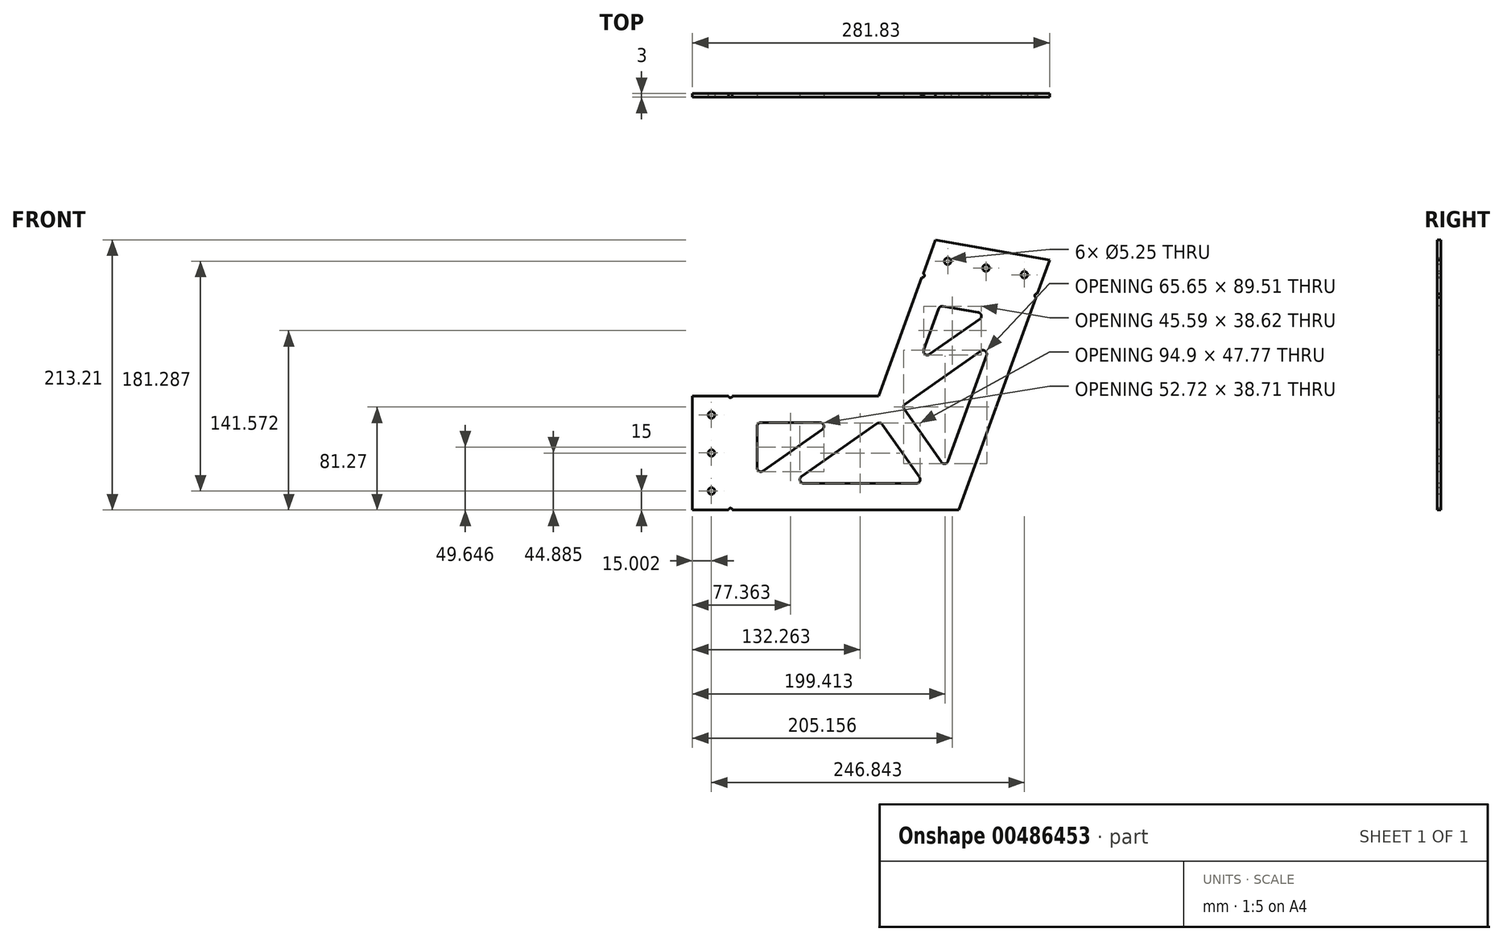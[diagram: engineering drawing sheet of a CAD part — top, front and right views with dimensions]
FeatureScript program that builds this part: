
annotation { "Feature Type Name" : "Feature", "Feature Type Description" : "" }
export const myFeature = defineFeature(function(context is Context, id is Id, definition is map)
    precondition{}
    {
        {
            var Q0;
            Q0=qCreatedBy(makeId("Front.planeOp"),FACE);
            var sketch = newSketch(context, id + "F0", { "sketchPlane" : qUnion([Q0])});
            skLineSegment(sketch, "E0", {"start": v(0, 0) * mm, "end": v(0, 0) * mm});
            skLineSegment(sketch, "E1", {"start": v(50, -65) * mm, "end": v(70.35, -9.1) * mm});
            skLineSegment(sketch, "E2", {"start": v(50, -65) * mm, "end": v(-9.5, -65) * mm});
            skLineSegment(sketch, "E3.0", {"start": v(29, -35) * mm, "end": v(40.35, -3.8) * mm});
            skLineSegment(sketch, "E4", {"start": v(-9.5, -35) * mm, "end": v(29, -35) * mm});
            skLineSegment(sketch, "E5.0", {"start": v(40.85, -22.91) * mm, "end": v(44.8, -12.04) * mm});
            skLineSegment(sketch, "E5.1", {"start": v(47.22, -52.19) * mm, "end": v(57.35, -24.34) * mm});
            skLineSegment(sketch, "E5.2", {"start": v(38.9, -58) * mm, "end": v(9.27, -58) * mm});
            skLineSegment(sketch, "E5.3", {"start": v(45.92, -11.4) * mm, "end": v(55.16, -13.03) * mm});
            skLineSegment(sketch, "E5.4", {"start": v(-3, -53.91) * mm, "end": v(-3, -43) * mm});
            skLineSegment(sketch, "E5.5", {"start": v(-2, -42) * mm, "end": v(13.57, -42) * mm});
            skLineSegment(sketch, "E6.0.left", {"start": v(-1.43, -54.73) * mm, "end": v(14.15, -43.83) * mm});
            skLineSegment(sketch, "E6.0.right", {"start": v(8.7, -56.2) * mm, "end": v(28.58, -42.27) * mm});
            skLineSegment(sketch, "E7.trimOffspring", {"start": v(42.36, -24.07) * mm, "end": v(55.56, -14.83) * mm});
            skLineSegment(sketch, "E8.0.left", {"start": v(35.7, -38.5) * mm, "end": v(45.46, -52.42) * mm});
            skLineSegment(sketch, "E8.0.right", {"start": v(29.97, -42.51) * mm, "end": v(39.72, -56.44) * mm});
            skLineSegment(sketch, "E9.trimOffspring", {"start": v(35.95, -37.1) * mm, "end": v(55.84, -23.18) * mm});
            skPoint(sketch, "E10.visualSharp", {"position": v(-3, -55.84) * mm});
            skArc(sketch, "E10.filletArc", {"start": v(-3, -53.91) * mm, "mid": v(-2.46, -54.8) * mm, "end": v(-1.43, -54.73) * mm});
            skPoint(sketch, "E11.visualSharp", {"position": v(-3, -42) * mm});
            skArc(sketch, "E11.filletArc", {"start": v(-2, -42) * mm, "mid": v(-2.7, -42.3) * mm, "end": v(-3, -43) * mm});
            skPoint(sketch, "E12.visualSharp", {"position": v(16.75, -42) * mm});
            skArc(sketch, "E12.filletArc", {"start": v(14.15, -43.83) * mm, "mid": v(14.53, -42.7) * mm, "end": v(13.57, -42) * mm});
            skPoint(sketch, "E13.visualSharp", {"position": v(29.4, -41.7) * mm});
            skArc(sketch, "E13.filletArc", {"start": v(29.97, -42.51) * mm, "mid": v(29.33, -42.1) * mm, "end": v(28.58, -42.27) * mm});
            skPoint(sketch, "E14.visualSharp", {"position": v(6.1, -58) * mm});
            skArc(sketch, "E14.filletArc", {"start": v(8.7, -56.2) * mm, "mid": v(8.32, -57.31) * mm, "end": v(9.27, -58) * mm});
            skPoint(sketch, "E15.visualSharp", {"position": v(40.83, -58) * mm});
            skArc(sketch, "E15.filletArc", {"start": v(38.9, -58) * mm, "mid": v(39.8, -57.47) * mm, "end": v(39.72, -56.44) * mm});
            skPoint(sketch, "E16.visualSharp", {"position": v(46.56, -54) * mm});
            skArc(sketch, "E16.filletArc", {"start": v(45.46, -52.42) * mm, "mid": v(46.4, -52.84) * mm, "end": v(47.22, -52.19) * mm});
            skPoint(sketch, "E17.visualSharp", {"position": v(35.14, -37.68) * mm});
            skArc(sketch, "E17.filletArc", {"start": v(35.95, -37.1) * mm, "mid": v(35.54, -37.75) * mm, "end": v(35.7, -38.5) * mm});
            skPoint(sketch, "E18.visualSharp", {"position": v(58.44, -21.36) * mm});
            skArc(sketch, "E18.filletArc", {"start": v(57.35, -24.34) * mm, "mid": v(57.02, -23.2) * mm, "end": v(55.84, -23.18) * mm});
            skPoint(sketch, "E19.visualSharp", {"position": v(45.1, -11.25) * mm});
            skArc(sketch, "E19.filletArc", {"start": v(45.92, -11.4) * mm, "mid": v(45.24, -11.52) * mm, "end": v(44.8, -12.04) * mm});
            skPoint(sketch, "E20.visualSharp", {"position": v(39.76, -25.9) * mm});
            skArc(sketch, "E20.filletArc", {"start": v(40.85, -22.91) * mm, "mid": v(41.18, -24.05) * mm, "end": v(42.36, -24.07) * mm});
            skPoint(sketch, "E21.visualSharp", {"position": v(57.54, -13.45) * mm});
            skArc(sketch, "E21.filletArc", {"start": v(55.56, -14.83) * mm, "mid": v(55.96, -13.8) * mm, "end": v(55.16, -13.03) * mm});
            skLineSegment(sketch, "E22", {"start": v(-10.5, -35) * mm, "end": v(-20, -35) * mm});
            skLineSegment(sketch, "E23", {"start": v(-10.5, -65) * mm, "end": v(-20, -65) * mm});
            skLineSegment(sketch, "E24", {"start": v(-20, -65) * mm, "end": v(-20, -35) * mm});
            skLineSegment(sketch, "E25", {"start": v(40.7, -2.87) * mm, "end": v(43.94, 6.06) * mm});
            skLineSegment(sketch, "E26", {"start": v(70.7, -8.16) * mm, "end": v(73.94, 0.77) * mm});
            skLineSegment(sketch, "E27", {"start": v(43.94, 6.06) * mm, "end": v(73.94, 0.77) * mm});
            skArc(sketch, "E28", {"start": v(-10.5, -35) * mm, "mid": v(-10, -35.5) * mm, "end": v(-9.5, -35) * mm});
            skArc(sketch, "E29", {"start": v(-9.5, -65) * mm, "mid": v(-10, -64.5) * mm, "end": v(-10.5, -65) * mm});
            skArc(sketch, "E30", {"start": v(40.35, -3.8) * mm, "mid": v(41, -3.5) * mm, "end": v(40.7, -2.87) * mm});
            skArc(sketch, "E31", {"start": v(70.7, -8.16) * mm, "mid": v(70.05, -8.46) * mm, "end": v(70.35, -9.1) * mm});
            skCircle(sketch, "E32", {"center": v(-15, -40) * mm, "radius": 0.88 * mm});
            skPoint(sketch, "E32.centerSnap0", {"position": v(-15.25, -35) * mm});
            skCircle(sketch, "E33", {"center": v(-15, -60) * mm, "radius": 0.88 * mm});
            skCircle(sketch, "E34", {"center": v(-15, -50) * mm, "radius": 0.88 * mm});
            skCircle(sketch, "E35", {"center": v(57.2, -1.36) * mm, "radius": 0.88 * mm});
            skCircle(sketch, "E36", {"center": v(47.13, 0.42) * mm, "radius": 0.88 * mm});
            skCircle(sketch, "E37", {"center": v(67.28, -3.13) * mm, "radius": 0.88 * mm});
            skSolve(sketch);
        }
        {
            var Q0;
            Q0=qSketchRegion(id+"F0",true);
            extrude(context, id + "F1", {"entities" : qUnion([Q0]), "oppositeDirection" : true, "depth" : 1 * mm, "offsetDistance" : 25 * mm});
        }
        {
            var Q0;
            Q0=makeQuery(id+"F1.opExtrude","SWEPT_BODY",BODY,{"disambiguationData":[OSD([sQuery(id+"F0.wireOp",EDGE,"E1"),sQuery(id+"F0.wireOp",EDGE,"E2"),sQuery(id+"F0.wireOp",EDGE,"E3.0"),sQuery(id+"F0.wireOp",EDGE,"E4"),sQuery(id+"F0.wireOp",EDGE,"E5.0"),sQuery(id+"F0.wireOp",EDGE,"E5.1"),sQuery(id+"F0.wireOp",EDGE,"E5.2"),sQuery(id+"F0.wireOp",EDGE,"E5.3"),sQuery(id+"F0.wireOp",EDGE,"E5.4"),sQuery(id+"F0.wireOp",EDGE,"E5.5"),sQuery(id+"F0.wireOp",EDGE,"E6.0.left"),sQuery(id+"F0.wireOp",EDGE,"E6.0.right"),sQuery(id+"F0.wireOp",EDGE,"E7.trimOffspring"),sQuery(id+"F0.wireOp",EDGE,"E8.0.left"),sQuery(id+"F0.wireOp",EDGE,"E8.0.right"),sQuery(id+"F0.wireOp",EDGE,"E9.trimOffspring"),sQuery(id+"F0.wireOp",EDGE,"E10.filletArc"),sQuery(id+"F0.wireOp",EDGE,"E11.filletArc"),sQuery(id+"F0.wireOp",EDGE,"E12.filletArc"),sQuery(id+"F0.wireOp",EDGE,"E13.filletArc"),sQuery(id+"F0.wireOp",EDGE,"E14.filletArc"),sQuery(id+"F0.wireOp",EDGE,"E15.filletArc"),sQuery(id+"F0.wireOp",EDGE,"E16.filletArc"),sQuery(id+"F0.wireOp",EDGE,"E17.filletArc"),sQuery(id+"F0.wireOp",EDGE,"E18.filletArc"),sQuery(id+"F0.wireOp",EDGE,"E19.filletArc"),sQuery(id+"F0.wireOp",EDGE,"E20.filletArc"),sQuery(id+"F0.wireOp",EDGE,"E21.filletArc"),sQuery(id+"F0.wireOp",EDGE,"E22"),sQuery(id+"F0.wireOp",EDGE,"E23"),sQuery(id+"F0.wireOp",EDGE,"E24"),sQuery(id+"F0.wireOp",EDGE,"E25"),sQuery(id+"F0.wireOp",EDGE,"E26"),sQuery(id+"F0.wireOp",EDGE,"E27"),sQuery(id+"F0.wireOp",EDGE,"E28"),sQuery(id+"F0.wireOp",EDGE,"E29"),sQuery(id+"F0.wireOp",EDGE,"E30"),sQuery(id+"F0.wireOp",EDGE,"E31")])]});
            var Q1;
            Q1=makeQuery(id+"F1.opExtrude","CAP_VERTEX",VERTEX,{"disambiguationData":[OSD([sQuery(id+"F0.wireOp",EDGE,"E3.0"),sQuery(id+"F0.wireOp",EDGE,"E4")])],"isStart":true});
            transform(context, id + "F2", {"entities" : qUnion([Q0]), "transformType" : TransformType.SCALE_UNIFORMLY, "scale" : 3, "scalePoint" : qUnion([Q1]), "makeCopy" : false});
        }
    });
